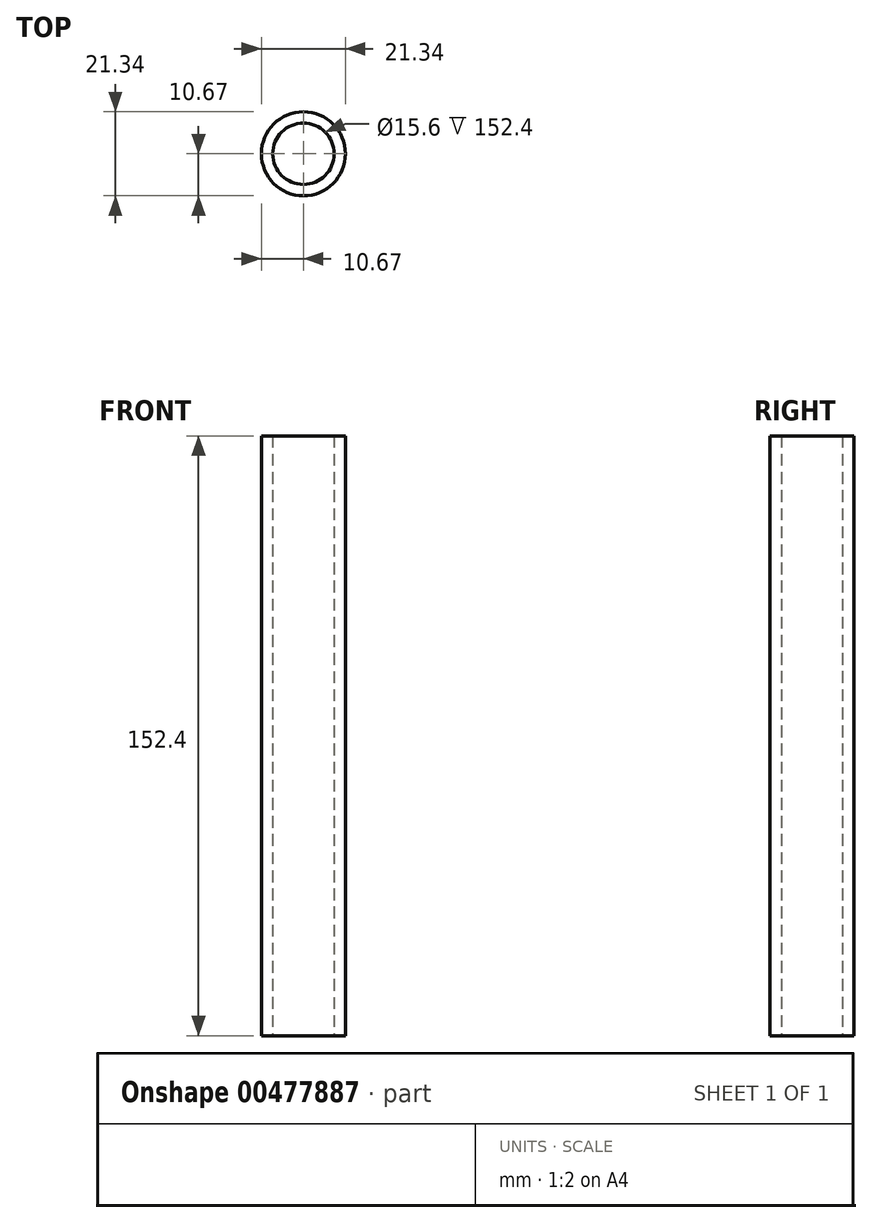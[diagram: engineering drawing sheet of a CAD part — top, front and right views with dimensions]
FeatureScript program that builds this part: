
annotation { "Feature Type Name" : "Feature", "Feature Type Description" : "" }
export const myFeature = defineFeature(function(context is Context, id is Id, definition is map)
    precondition{}
    {
        {
            var Q0;
            Q0=qCreatedBy(makeId("Top.planeOp"),FACE);
            var sketch = newSketch(context, id + "F0", { "sketchPlane" : qUnion([Q0])});
            skCircle(sketch, "E0", {"center": v(0, 0) * mm, "radius": 7.8 * mm});
            skCircle(sketch, "E1", {"center": v(0, 0) * mm, "radius": 10.67 * mm});
            skLineSegment(sketch, "E2", {"start": v(7.8, 0) * mm, "end": v(10.67, 0) * mm, "construction": true});
            skSolve(sketch);
        }
        {
            var Q0;
            Q0=makeQuery(id+"F0.imprint","IMPRINT",FACE,{"disambiguationData":[TD([[makeQuery(id+"F0.imprint","IMPRINT",EDGE,{"derivedFrom":sQuery(id+"F0.wireOp",EDGE,"E0")}),-1.0]])]});
            extrude(context, id + "F1", {"entities" : qUnion([Q0]), "depth" : 152.4 * mm});
        }
    });
